# Revit family: ps-rp50160ka20_50hz
name_source: partatom
category: 機械設備
units: mm (PartAtom-declared; Revit-internal decimal feet)

## family parameters
OmniClass タイトル = Split System Air Conditioning Units
OmniClass 番号 = 23.75.10.24.21.27.27
パーツ タイプ = 標準
ロード時にボイドで切り取り = いいえ
丸型コネクタ寸法 = 直径を使用
作業面ベース = いいえ
共有 = いいえ
常に垂直 = はい
部屋計算ポイント = はい

## types (8) — shared parameters
Clearance Back = 5 mm
Clearance Bottom = 0 mm
Clearance Front = 1000 mm
Clearance Left = 100 mm
Clearance Right = 100 mm
Clearance Top = 300 mm
IfcExportAs = IfcUnitaryEquipmentType
IfcExportType = AIRCONDITIONINGUNIT
OmniClassCode = 23-33 17 13 11
URL = https://www.mitsubishielectric.co.jp
Uniclass2015Code = Pr_70_65_03_84
Uniclass2015Title = Split coil remote air cooled condensing units
Uniclass2015Version = Systems v1.9
ケーブルサイズ = 0 mm
サービススペース = はい
ドレン管径 = 20.00 mm
ドレン管径 (外径) = 26 mm
パネルマテリアル = <カテゴリ別>
仕様書バージョン = Version1.0
企業コード = 108420
冷媒管径 = 100.00 mm
冷媒高低圧ガス管径 = 0.00 mm
冷媒，ドレン配管用ノックアウト穴正面-X2 = 20 mm
分類コード = 5.0053E+13
加湿給水管径 = 0.00 mm
参照している仕様書等のバージョン = 公共建築工事標準仕様書（機械設備工事編）平成31年度版
周波数 = 50 Hz
呼称 = 室内機_床置（露出）立形（直吹）
始動方式 = 直入
形式 = 床置（露出）立形
推奨ブレーカー容量 = 0 A
本体マテリアル = <カテゴリ別>
極数 = 1
法定耐用年数 = 6
発停方法 = 付属スイッチ
相 = 1
積算_科目 = 1 空気調和設備
符号 = PAC_FRV
製品出荷対象 = 国内
製造元 = 三菱電機株式会社
設置方法 = 床置形
設計冷房能力 = 0 kW
設計冷房能力_顕熱 = 0 kW
設計暖房能力 = 0.00 kW
説明 = 店舗・事務所用パッケージエアコン(Mr.SLIM) 床置形
負荷分類 = 3_ファン類
運転質量 = 0.00 kg
電圧 = 0 V
電機品箱位置W = 22 mm
電源_H = 0 mm
電線用ノックアウト穴Z2 = 90 mm
zero-valued in all types: 価格, 有効加湿量

## per-type parameters (varying)
- 床置_PS-RP50KA20: A=173 mm; B=797 mm; Depth=270 mm; Height=1700 mm; MAX風量=840.0 m³/h; MID風量=780.0 m³/h; MIN風量=720.0 m³/h; Width=470 mm; ドレン管径-X=25 mm; ドレン管径-Y=210 mm; 冷媒ガス管位置-X=78 mm; 冷媒ガス管位置-Y=186 mm; 冷媒ガス管位置-Z=402 mm; 冷媒ガス管径=12.70 mm; 冷媒液管位置-X=45 mm; 冷媒液管位置-Y=201 mm; 冷媒液管位置-Z=550 mm; 冷媒液管径=6.35 mm; 冷媒管径符号=Ac; 冷媒，ドレン配管用ノックアウト穴側面-Y=180 mm; 冷媒，ドレン配管用ノックアウト穴側面-Z=110 mm; 冷媒，ドレン配管用ノックアウト穴正面-X1=75 mm; 冷媒，ドレン配管用ノックアウト穴正面-Z=105 mm; 冷房能力=4.5 kW; 吊り位置X_1=200 mm; 吊り位置X_2=280 mm; 吊り位置X_3=80 mm; 吊り位置Y_1=55 mm; 吊り位置Y_2=145 mm; 吊り位置y_3=175 mm; 吸込口幅=405 mm; 吸込口高さ=585 mm; 吹出口幅=400 mm; 吹出口高さ=230 mm; 暖房能力=5.00 kW; 構成品番=PS-RP50KA20; 消費電力=0.09 kW; 消費電力_冷房=0.09 kW; 消費電力_暖房=0.08 kW; 製品質量=35.00 kg; 質量=42.00 kg; 転倒防止金具幅=180 mm; 電動機出力_送風機=0.05 kW; 電機品箱D=61 mm; 電機品箱H=151 mm; 電機品箱W=348 mm; 電機品箱位置D=170 mm; 電機品箱位置H=641 mm; 電線用ノックアウト穴Y=110 mm; 電線用ノックアウト穴Z1=130 mm; 音響パワーレベル(dB)=56; 音響パワーレベル_中 (dB)=54; 音響パワーレベル_弱 (dB)=52; 音響パワーレベル_強 (dB)=56; 風量=840.0 m³/h; 風量_中 (㎥/min)=13; 風量_弱 (㎥/min)=12; 風量_強 (㎥/min)=14
- 床置_PS-RP56KA20: A=173 mm; B=797 mm; Depth=270 mm; Height=1700 mm; MAX風量=840.0 m³/h; MID風量=780.0 m³/h; MIN風量=720.0 m³/h; Width=470 mm; ドレン管径-X=25 mm; ドレン管径-Y=210 mm; 冷媒ガス管位置-X=78 mm; 冷媒ガス管位置-Y=186 mm; 冷媒ガス管位置-Z=402 mm; 冷媒ガス管径=12.70 mm; 冷媒液管位置-X=45 mm; 冷媒液管位置-Y=201 mm; 冷媒液管位置-Z=550 mm; 冷媒液管径=6.35 mm; 冷媒管径符号=Ac; 冷媒，ドレン配管用ノックアウト穴側面-Y=180 mm; 冷媒，ドレン配管用ノックアウト穴側面-Z=110 mm; 冷媒，ドレン配管用ノックアウト穴正面-X1=75 mm; 冷媒，ドレン配管用ノックアウト穴正面-Z=105 mm; 冷房能力=5 kW; 吊り位置X_1=200 mm; 吊り位置X_2=280 mm; 吊り位置X_3=80 mm; 吊り位置Y_1=55 mm; 吊り位置Y_2=145 mm; 吊り位置y_3=175 mm; 吸込口幅=405 mm; 吸込口高さ=585 mm; 吹出口幅=400 mm; 吹出口高さ=230 mm; 暖房能力=5.60 kW; 構成品番=PS-RP56KA20; 消費電力=0.09 kW; 消費電力_冷房=0.09 kW; 消費電力_暖房=0.08 kW; 製品質量=35.00 kg; 質量=42.00 kg; 転倒防止金具幅=180 mm; 電動機出力_送風機=0.05 kW; 電機品箱D=61 mm; 電機品箱H=151 mm; 電機品箱W=348 mm; 電機品箱位置D=170 mm; 電機品箱位置H=641 mm; 電線用ノックアウト穴Y=110 mm; 電線用ノックアウト穴Z1=130 mm; 音響パワーレベル(dB)=56; 音響パワーレベル_中 (dB)=54; 音響パワーレベル_弱 (dB)=52; 音響パワーレベル_強 (dB)=56; 風量=840.0 m³/h; 風量_中 (㎥/min)=13; 風量_弱 (㎥/min)=12; 風量_強 (㎥/min)=14
- 床置_PS-RP63KA20: A=173 mm; B=797 mm; Depth=270 mm; Height=1700 mm; MAX風量=900.0 m³/h; MID風量=840.0 m³/h; MIN風量=780.0 m³/h; Width=470 mm; ドレン管径-X=25 mm; ドレン管径-Y=210 mm; 冷媒ガス管位置-X=78 mm; 冷媒ガス管位置-Y=186 mm; 冷媒ガス管位置-Z=402 mm; 冷媒ガス管径=12.70 mm; 冷媒液管位置-X=45 mm; 冷媒液管位置-Y=201 mm; 冷媒液管位置-Z=550 mm; 冷媒液管径=6.35 mm; 冷媒管径符号=Ac; 冷媒，ドレン配管用ノックアウト穴側面-Y=180 mm; 冷媒，ドレン配管用ノックアウト穴側面-Z=110 mm; 冷媒，ドレン配管用ノックアウト穴正面-X1=75 mm; 冷媒，ドレン配管用ノックアウト穴正面-Z=105 mm; 冷房能力=5.6 kW; 吊り位置X_1=200 mm; 吊り位置X_2=280 mm; 吊り位置X_3=80 mm; 吊り位置Y_1=55 mm; 吊り位置Y_2=145 mm; 吊り位置y_3=175 mm; 吸込口幅=405 mm; 吸込口高さ=585 mm; 吹出口幅=400 mm; 吹出口高さ=230 mm; 暖房能力=6.30 kW; 構成品番=PS-RP63KA20; 消費電力=0.09 kW; 消費電力_冷房=0.09 kW; 消費電力_暖房=0.08 kW; 製品質量=35.00 kg; 質量=42.00 kg; 転倒防止金具幅=180 mm; 電動機出力_送風機=0.05 kW; 電機品箱D=61 mm; 電機品箱H=151 mm; 電機品箱W=348 mm; 電機品箱位置D=170 mm; 電機品箱位置H=641 mm; 電線用ノックアウト穴Y=110 mm; 電線用ノックアウト穴Z1=130 mm; 音響パワーレベル(dB)=56; 音響パワーレベル_中 (dB)=54; 音響パワーレベル_弱 (dB)=52; 音響パワーレベル_強 (dB)=56; 風量=900.0 m³/h; 風量_中 (㎥/min)=14; 風量_弱 (㎥/min)=13; 風量_強 (㎥/min)=15
- 床置_PS-RP71KA20: A=173 mm; B=797 mm; Depth=270 mm; Height=1700 mm; MAX風量=900.0 m³/h; MID風量=840.0 m³/h; MIN風量=780.0 m³/h; Width=470 mm; ドレン管径-X=25 mm; ドレン管径-Y=210 mm; 冷媒ガス管位置-X=78 mm; 冷媒ガス管位置-Y=186 mm; 冷媒ガス管位置-Z=402 mm; 冷媒ガス管径=15.88 mm; 冷媒液管位置-X=45 mm; 冷媒液管位置-Y=201 mm; 冷媒液管位置-Z=550 mm; 冷媒液管径=9.52 mm; 冷媒管径符号=Bd; 冷媒，ドレン配管用ノックアウト穴側面-Y=180 mm; 冷媒，ドレン配管用ノックアウト穴側面-Z=110 mm; 冷媒，ドレン配管用ノックアウト穴正面-X1=75 mm; 冷媒，ドレン配管用ノックアウト穴正面-Z=105 mm; 冷房能力=6.3 kW; 吊り位置X_1=200 mm; 吊り位置X_2=280 mm; 吊り位置X_3=80 mm; 吊り位置Y_1=55 mm; 吊り位置Y_2=145 mm; 吊り位置y_3=175 mm; 吸込口幅=405 mm; 吸込口高さ=585 mm; 吹出口幅=400 mm; 吹出口高さ=230 mm; 暖房能力=7.10 kW; 構成品番=PS-RP71KA20; 消費電力=0.09 kW; 消費電力_冷房=0.09 kW; 消費電力_暖房=0.08 kW; 製品質量=35.00 kg; 質量=42.00 kg; 転倒防止金具幅=180 mm; 電動機出力_送風機=0.05 kW; 電機品箱D=61 mm; 電機品箱H=151 mm; 電機品箱W=348 mm; 電機品箱位置D=170 mm; 電機品箱位置H=641 mm; 電線用ノックアウト穴Y=110 mm; 電線用ノックアウト穴Z1=130 mm; 音響パワーレベル(dB)=57; 音響パワーレベル_中 (dB)=55; 音響パワーレベル_弱 (dB)=52; 音響パワーレベル_強 (dB)=57; 風量=900.0 m³/h; 風量_中 (㎥/min)=14; 風量_弱 (㎥/min)=13; 風量_強 (㎥/min)=15
- 床置_PS-RP80KA20: A=173 mm; B=797 mm; Depth=270 mm; Height=1700 mm; MAX風量=900.0 m³/h; MID風量=840.0 m³/h; MIN風量=780.0 m³/h; Width=470 mm; ドレン管径-X=25 mm; ドレン管径-Y=210 mm; 冷媒ガス管位置-X=78 mm; 冷媒ガス管位置-Y=186 mm; 冷媒ガス管位置-Z=402 mm; 冷媒ガス管径=15.88 mm; 冷媒液管位置-X=45 mm; 冷媒液管位置-Y=201 mm; 冷媒液管位置-Z=550 mm; 冷媒液管径=9.52 mm; 冷媒管径符号=Bd; 冷媒，ドレン配管用ノックアウト穴側面-Y=180 mm; 冷媒，ドレン配管用ノックアウト穴側面-Z=110 mm; 冷媒，ドレン配管用ノックアウト穴正面-X1=75 mm; 冷媒，ドレン配管用ノックアウト穴正面-Z=105 mm; 冷房能力=7.1 kW; 吊り位置X_1=200 mm; 吊り位置X_2=280 mm; 吊り位置X_3=80 mm; 吊り位置Y_1=55 mm; 吊り位置Y_2=145 mm; 吊り位置y_3=175 mm; 吸込口幅=405 mm; 吸込口高さ=585 mm; 吹出口幅=400 mm; 吹出口高さ=230 mm; 暖房能力=8.00 kW; 構成品番=PS-RP80KA20; 消費電力=0.09 kW; 消費電力_冷房=0.09 kW; 消費電力_暖房=0.08 kW; 製品質量=35.00 kg; 質量=42.00 kg; 転倒防止金具幅=180 mm; 電動機出力_送風機=0.05 kW; 電機品箱D=61 mm; 電機品箱H=151 mm; 電機品箱W=348 mm; 電機品箱位置D=170 mm; 電機品箱位置H=641 mm; 電線用ノックアウト穴Y=110 mm; 電線用ノックアウト穴Z1=130 mm; 音響パワーレベル(dB)=57; 音響パワーレベル_中 (dB)=55; 音響パワーレベル_弱 (dB)=52; 音響パワーレベル_強 (dB)=57; 風量=900.0 m³/h; 風量_中 (㎥/min)=14; 風量_弱 (㎥/min)=13; 風量_強 (㎥/min)=15
- 床置_PS-RP112KA20: A=181 mm; B=834 mm; Depth=360 mm; Height=1900 mm; MAX風量=1800.0 m³/h; MID風量=1620.0 m³/h; MIN風量=1440.0 m³/h; Width=600 mm; ドレン管径-X=27 mm; ドレン管径-Y=289 mm; 冷媒ガス管位置-X=95 mm; 冷媒ガス管位置-Y=261 mm; 冷媒ガス管位置-Z=480 mm; 冷媒ガス管径=15.88 mm; 冷媒液管位置-X=48 mm; 冷媒液管位置-Y=261 mm; 冷媒液管位置-Z=590 mm; 冷媒液管径=9.52 mm; 冷媒管径符号=Bd; 冷媒，ドレン配管用ノックアウト穴側面-Y=260 mm; 冷媒，ドレン配管用ノックアウト穴側面-Z=115 mm; 冷媒，ドレン配管用ノックアウト穴正面-X1=105 mm; 冷媒，ドレン配管用ノックアウト穴正面-Z=110 mm; 冷房能力=10 kW; 吊り位置X_1=218 mm; 吊り位置X_2=277 mm; 吊り位置X_3=99 mm; 吊り位置Y_1=77 mm; 吊り位置Y_2=201 mm; 吊り位置y_3=254 mm; 吸込口幅=524 mm; 吸込口高さ=599 mm; 吹出口幅=520 mm; 吹出口高さ=260 mm; 暖房能力=11.20 kW; 構成品番=PS-RP112KA20; 消費電力=0.21 kW; 消費電力_冷房=0.21 kW; 消費電力_暖房=0.20 kW; 製品質量=49.00 kg; 質量=58.80 kg; 転倒防止金具幅=260 mm; 電動機出力_送風機=0.16 kW; 電機品箱D=66 mm; 電機品箱H=123 mm; 電機品箱W=461 mm; 電機品箱位置D=245 mm; 電機品箱位置H=714 mm; 電線用ノックアウト穴Y=190 mm; 電線用ノックアウト穴Z1=140 mm; 音響パワーレベル(dB)=63; 音響パワーレベル_中 (dB)=61; 音響パワーレベル_弱 (dB)=57; 音響パワーレベル_強 (dB)=63; 風量=1800.0 m³/h; 風量_中 (㎥/min)=27; 風量_弱 (㎥/min)=24; 風量_強 (㎥/min)=30
- 床置_PS-RP140KA20: A=181 mm; B=834 mm; Depth=360 mm; Height=1900 mm; MAX風量=1800.0 m³/h; MID風量=1620.0 m³/h; MIN風量=1440.0 m³/h; Width=600 mm; ドレン管径-X=27 mm; ドレン管径-Y=289 mm; 冷媒ガス管位置-X=95 mm; 冷媒ガス管位置-Y=261 mm; 冷媒ガス管位置-Z=480 mm; 冷媒ガス管径=15.88 mm; 冷媒液管位置-X=48 mm; 冷媒液管位置-Y=261 mm; 冷媒液管位置-Z=590 mm; 冷媒液管径=9.52 mm; 冷媒管径符号=Bd; 冷媒，ドレン配管用ノックアウト穴側面-Y=260 mm; 冷媒，ドレン配管用ノックアウト穴側面-Z=115 mm; 冷媒，ドレン配管用ノックアウト穴正面-X1=105 mm; 冷媒，ドレン配管用ノックアウト穴正面-Z=110 mm; 冷房能力=12.5 kW; 吊り位置X_1=218 mm; 吊り位置X_2=277 mm; 吊り位置X_3=99 mm; 吊り位置Y_1=77 mm; 吊り位置Y_2=201 mm; 吊り位置y_3=254 mm; 吸込口幅=524 mm; 吸込口高さ=599 mm; 吹出口幅=520 mm; 吹出口高さ=260 mm; 暖房能力=14.00 kW; 構成品番=PS-RP140KA20; 消費電力=0.21 kW; 消費電力_冷房=0.21 kW; 消費電力_暖房=0.20 kW; 製品質量=49.00 kg; 質量=58.80 kg; 転倒防止金具幅=260 mm; 電動機出力_送風機=0.16 kW; 電機品箱D=66 mm; 電機品箱H=123 mm; 電機品箱W=461 mm; 電機品箱位置D=245 mm; 電機品箱位置H=714 mm; 電線用ノックアウト穴Y=190 mm; 電線用ノックアウト穴Z1=140 mm; 音響パワーレベル(dB)=63; 音響パワーレベル_中 (dB)=61; 音響パワーレベル_弱 (dB)=57; 音響パワーレベル_強 (dB)=63; 風量=1800.0 m³/h; 風量_中 (㎥/min)=27; 風量_弱 (㎥/min)=24; 風量_強 (㎥/min)=30
- 床置_PS-RP160KA20: A=181 mm; B=834 mm; Depth=360 mm; Height=1900 mm; MAX風量=1800.0 m³/h; MID風量=1620.0 m³/h; MIN風量=1440.0 m³/h; Width=600 mm; ドレン管径-X=27 mm; ドレン管径-Y=289 mm; 冷媒ガス管位置-X=95 mm; 冷媒ガス管位置-Y=261 mm; 冷媒ガス管位置-Z=480 mm; 冷媒ガス管径=15.88 mm; 冷媒液管位置-X=48 mm; 冷媒液管位置-Y=261 mm; 冷媒液管位置-Z=590 mm; 冷媒液管径=9.52 mm; 冷媒管径符号=Bd; 冷媒，ドレン配管用ノックアウト穴側面-Y=260 mm; 冷媒，ドレン配管用ノックアウト穴側面-Z=115 mm; 冷媒，ドレン配管用ノックアウト穴正面-X1=105 mm; 冷媒，ドレン配管用ノックアウト穴正面-Z=110 mm; 冷房能力=14 kW; 吊り位置X_1=218 mm; 吊り位置X_2=277 mm; 吊り位置X_3=99 mm; 吊り位置Y_1=77 mm; 吊り位置Y_2=201 mm; 吊り位置y_3=254 mm; 吸込口幅=524 mm; 吸込口高さ=599 mm; 吹出口幅=520 mm; 吹出口高さ=260 mm; 暖房能力=16.00 kW; 構成品番=PS-RP160KA20; 消費電力=0.21 kW; 消費電力_冷房=0.21 kW; 消費電力_暖房=0.20 kW; 製品質量=49.00 kg; 質量=58.80 kg; 転倒防止金具幅=260 mm; 電動機出力_送風機=0.16 kW; 電機品箱D=66 mm; 電機品箱H=123 mm; 電機品箱W=461 mm; 電機品箱位置D=245 mm; 電機品箱位置H=714 mm; 電線用ノックアウト穴Y=190 mm; 電線用ノックアウト穴Z1=140 mm; 音響パワーレベル(dB)=64; 音響パワーレベル_中 (dB)=62; 音響パワーレベル_弱 (dB)=59; 音響パワーレベル_強 (dB)=64; 風量=1800.0 m³/h; 風量_中 (㎥/min)=27; 風量_弱 (㎥/min)=24; 風量_強 (㎥/min)=30
